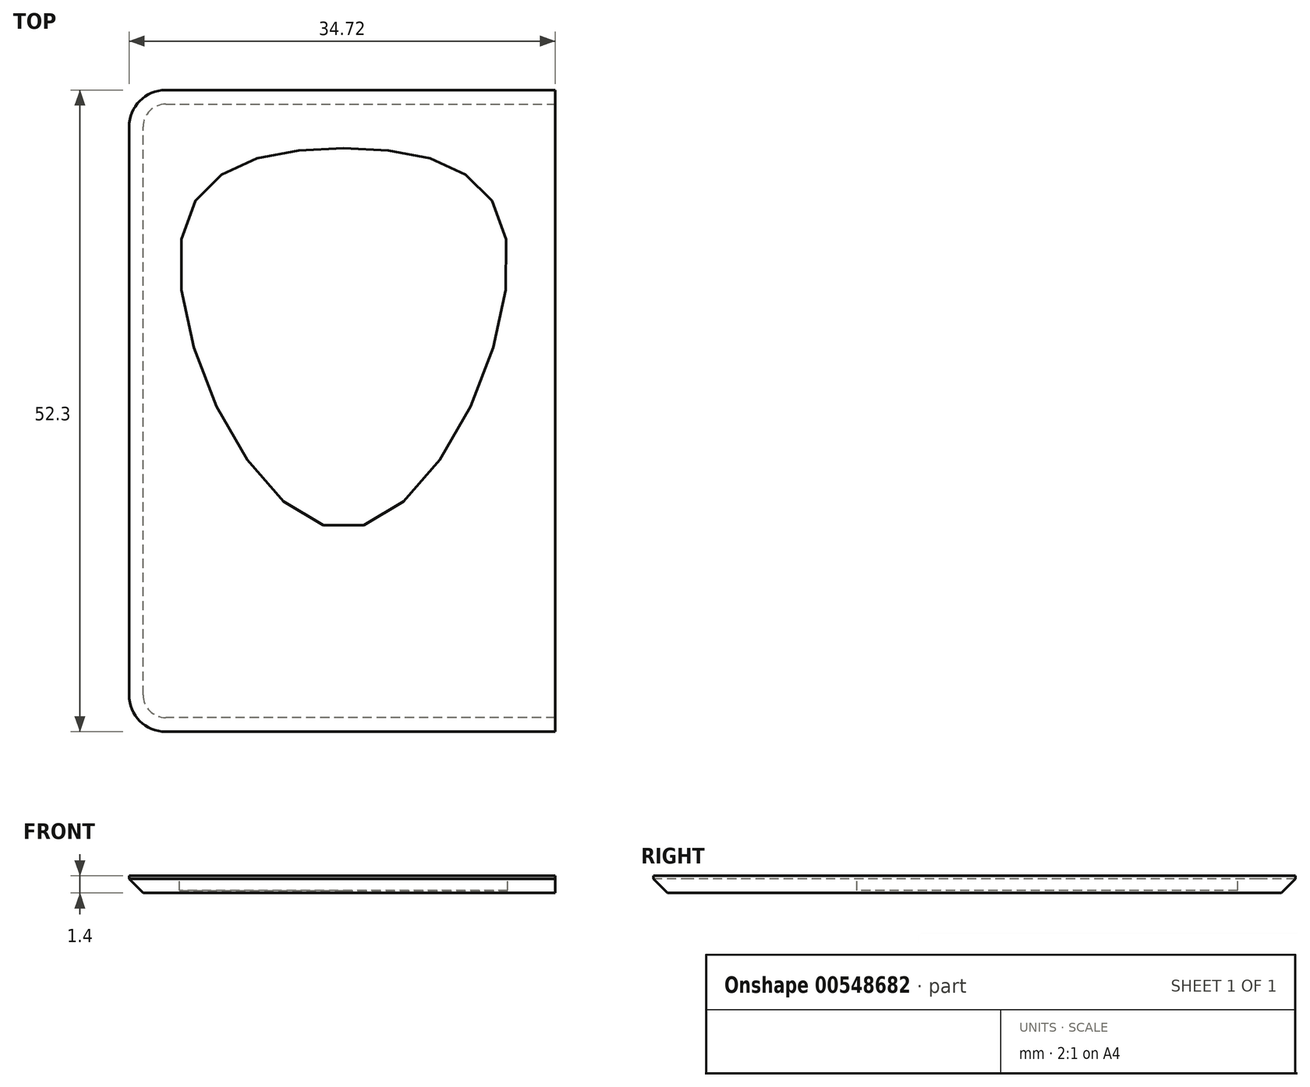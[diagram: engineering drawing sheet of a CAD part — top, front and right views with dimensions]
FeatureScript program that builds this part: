
annotation { "Feature Type Name" : "Feature", "Feature Type Description" : "" }
export const myFeature = defineFeature(function(context is Context, id is Id, definition is map)
    precondition{}
    {
        {
            var Q0;
            Q0=qCreatedBy(makeId("Top.planeOp"),FACE);
            var sketch = newSketch(context, id + "F0", { "sketchPlane" : qUnion([Q0])});
            skLineSegment(sketch, "E0.bottom", {"start": v(3, 0) * mm, "end": v(81.7, 0) * mm});
            skLineSegment(sketch, "E0.top", {"start": v(3, 52.3) * mm, "end": v(81.7, 52.3) * mm});
            skLineSegment(sketch, "E0.left", {"start": v(0, 3) * mm, "end": v(0, 49.3) * mm});
            skLineSegment(sketch, "E0.right", {"start": v(84.7, 3) * mm, "end": v(84.7, 49.3) * mm});
            skPoint(sketch, "E1.visualSharp", {"position": v(0, 0) * mm});
            skArc(sketch, "E1.filletArc", {"start": v(0, 3) * mm, "mid": v(0.88, 0.88) * mm, "end": v(3, 0) * mm});
            skPoint(sketch, "E2.visualSharp", {"position": v(0, 52.3) * mm});
            skArc(sketch, "E2.filletArc", {"start": v(3, 52.3) * mm, "mid": v(0.88, 51.42) * mm, "end": v(0, 49.3) * mm});
            skPoint(sketch, "E3.visualSharp", {"position": v(84.7, 52.3) * mm});
            skArc(sketch, "E3.filletArc", {"start": v(84.7, 49.3) * mm, "mid": v(83.82, 51.42) * mm, "end": v(81.7, 52.3) * mm});
            skPoint(sketch, "E4.visualSharp", {"position": v(84.7, 0) * mm});
            skArc(sketch, "E4.filletArc", {"start": v(81.7, 0) * mm, "mid": v(83.82, 0.88) * mm, "end": v(84.7, 3) * mm});
            skSolve(sketch);
        }
        {
            var Q0;
            Q0=qSketchRegion(id+"F0",true);
            extrude(context, id + "F1", {"entities" : qUnion([Q0]), "depth" : 1.4 * mm, "offsetDistance" : 25 * mm});
        }
        {
            var Q0;
            Q0=makeQuery(id+"F1.opExtrude","CAP_FACE",FACE,{"disambiguationData":[OSD([sQuery(id+"F0.wireOp",EDGE,"E0.bottom"),sQuery(id+"F0.wireOp",EDGE,"E0.top"),sQuery(id+"F0.wireOp",EDGE,"E0.left"),sQuery(id+"F0.wireOp",EDGE,"E0.right")])],"isStart":false});
            var sketch = newSketch(context, id + "F2", { "sketchPlane" : qUnion([Q0])});
            skLineSegment(sketch, "E5.0", {"start": v(0, 3) * mm, "end": v(0, 49.3) * mm});
            skArc(sketch, "E6.0", {"start": v(0, 3) * mm, "mid": v(0.88, 0.88) * mm, "end": v(3, 0) * mm});
            skLineSegment(sketch, "E7.0", {"start": v(3, 0) * mm, "end": v(81.7, 0) * mm});
            skArc(sketch, "E8.0", {"start": v(81.7, 0) * mm, "mid": v(83.82, 0.88) * mm, "end": v(84.7, 3) * mm});
            skLineSegment(sketch, "E9.0", {"start": v(84.7, 3) * mm, "end": v(84.7, 49.3) * mm});
            skLineSegment(sketch, "E10.0", {"start": v(3, 52.3) * mm, "end": v(81.7, 52.3) * mm});
            skArc(sketch, "E11.0", {"start": v(84.7, 49.3) * mm, "mid": v(83.82, 51.42) * mm, "end": v(81.7, 52.3) * mm});
            skLineSegment(sketch, "E12", {"start": v(17.48, 16.58) * mm, "end": v(17.48, 47.58) * mm, "construction": true});
            skFitSpline(sketch, "E13", {"points": [v(17.48, 47.58) * mm, v(30.63, 40.58) * mm, v(17.48, 16.58) * mm, v(4.33, 40.58) * mm, v(17.48, 47.58) * mm]});
            skSolve(sketch);
        }
        {
            var Q0;
            Q0=makeQuery(id+"F1.opExtrude","CAP_EDGE",EDGE,{"disambiguationData":[OSD([sQuery(id+"F0.wireOp",EDGE,"E0.bottom")])],"isStart":true});
            chamfer(context, id + "F3", {"entities" : qUnion([Q0]), "width" : 1.15 * mm, "tangentPropagation" : true});
        }
        {
            var Q0;
            Q0=makeQuery(id+"F2.imprint","IMPRINT",FACE,{"disambiguationData":[TD([[makeQuery(id+"F2.imprint","IMPRINT",EDGE,{"derivedFrom":sQuery(id+"F2.wireOp",EDGE,"E13")}),-1.0]])]});
            extrude(context, id + "F4", {"entities" : qUnion([Q0]), "operationType" : NewBodyOperationType.REMOVE, "oppositeDirection" : true, "depth" : 1.2 * mm, "offsetDistance" : 25 * mm});
        }
        {
            var Q0;
            Q0=makeQuery(id+"F1.opExtrude","CAP_FACE",FACE,{"disambiguationData":[OSD([sQuery(id+"F0.wireOp",EDGE,"E0.bottom"),sQuery(id+"F0.wireOp",EDGE,"E0.top"),sQuery(id+"F0.wireOp",EDGE,"E0.left"),sQuery(id+"F0.wireOp",EDGE,"E0.right"),sQuery(id+"F0.wireOp",EDGE,"E1.filletArc"),sQuery(id+"F0.wireOp",EDGE,"E2.filletArc"),sQuery(id+"F0.wireOp",EDGE,"E3.filletArc"),sQuery(id+"F0.wireOp",EDGE,"E4.filletArc")])],"isStart":false});
            var sketch = newSketch(context, id + "F5", { "sketchPlane" : qUnion([Q0])});
            skLineSegment(sketch, "E14.bottom", {"start": v(34.72, 56.57) * mm, "end": v(95.28, 56.57) * mm});
            skLineSegment(sketch, "E14.top", {"start": v(34.72, -13.65) * mm, "end": v(95.28, -13.65) * mm});
            skLineSegment(sketch, "E14.left", {"start": v(34.72, 56.57) * mm, "end": v(34.72, -13.65) * mm});
            skLineSegment(sketch, "E14.right", {"start": v(95.28, 56.57) * mm, "end": v(95.28, -13.65) * mm});
            skSolve(sketch);
        }
        {
            var Q0;
            Q0 = qSketchRegion(id + "F5", true);
            extrude(context, id + "F6", {"entities" : qUnion([Q0]), "operationType" : NewBodyOperationType.REMOVE, "oppositeDirection" : true, "depth" : 25 * mm, "offsetDistance" : 25 * mm});
        }
    });
